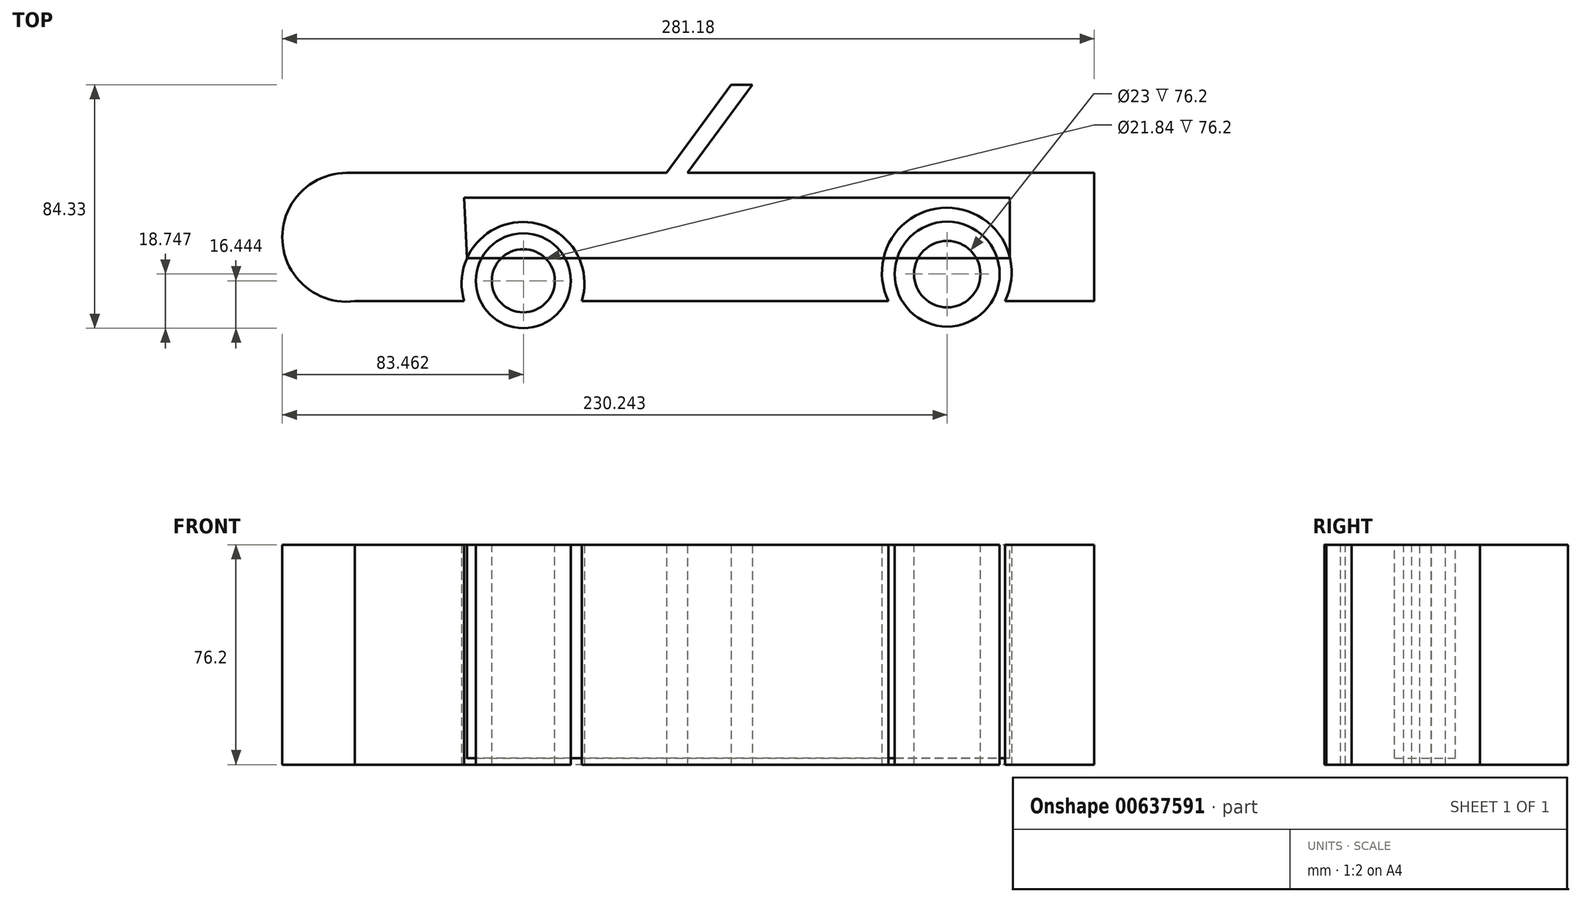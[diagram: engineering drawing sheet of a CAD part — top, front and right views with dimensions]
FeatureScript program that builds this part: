
annotation { "Feature Type Name" : "Feature", "Feature Type Description" : "" }
export const myFeature = defineFeature(function(context is Context, id is Id, definition is map)
    precondition{}
    {
        {
            var Q0;
            Q0=qCreatedBy(makeId("Top.planeOp"),FACE);
            var sketch = newSketch(context, id + "F0", { "sketchPlane" : qUnion([Q0])});
            skLineSegment(sketch, "E0", {"start": v(-131.9, 16.49) * mm, "end": v(-62.3, 16.49) * mm});
            skLineSegment(sketch, "E1", {"start": v(-62.3, 16.49) * mm, "end": v(-39.9, 47.02) * mm});
            skLineSegment(sketch, "E2", {"start": v(-131.9, 16.49) * mm, "end": v(-173.01, 16.49) * mm});
            skLineSegment(sketch, "E3", {"start": v(-170.17, -27.93) * mm, "end": v(-132.31, -27.93) * mm});
            skArc(sketch, "E4", {"start": v(-173.01, 16.49) * mm, "mid": v(-195.27, -7.24) * mm, "end": v(-170.17, -27.93) * mm});
            skArc(sketch, "E5", {"start": v(-91.6, -27.93) * mm, "mid": v(-111.96, -0.49) * mm, "end": v(-132.31, -27.93) * mm});
            skLineSegment(sketch, "E6", {"start": v(-91.6, -27.93) * mm, "end": v(14.63, -27.93) * mm});
            skArc(sketch, "E7", {"start": v(54.93, -27.93) * mm, "mid": v(34.78, 4.42) * mm, "end": v(14.63, -27.93) * mm});
            skLineSegment(sketch, "E8", {"start": v(54.93, -27.93) * mm, "end": v(87.5, -27.93) * mm});
            skLineSegment(sketch, "E9", {"start": v(-62.3, 16.49) * mm, "end": v(85.87, 16.49) * mm});
            skLineSegment(sketch, "E10", {"start": v(85.87, 16.49) * mm, "end": v(85.87, -27.93) * mm});
            skLineSegment(sketch, "E11", {"start": v(-39.9, 47.02) * mm, "end": v(-32.57, 47.02) * mm});
            skLineSegment(sketch, "E12", {"start": v(-32.57, 47.02) * mm, "end": v(-54.96, 16.49) * mm});
            skSolve(sketch);
        }
        {
            var Q0;
            {var subQ3=sQuery(id+"F0.wireOp",EDGE,"E0");Q0=makeQuery(id+"F0.imprint","IMPRINT",FACE,{"disambiguationData":[TD([[makeQuery(id+"F0.imprint","IMPRINT",EDGE,{"derivedFrom":subQ3}),-1.0]])]});}
            var Q1;
            {var subQ0=sQuery(id+"F0.wireOp",EDGE,"E1");Q1=makeQuery(id+"F0.imprint","IMPRINT",FACE,{"disambiguationData":[TD([[makeQuery(id+"F0.imprint","IMPRINT",EDGE,{"derivedFrom":subQ0}),-1.0]])]});}
            extrude(context, id + "F1", {"entities" : qUnion([Q0, Q1]), "depth" : 76.2 * mm, "offsetDistance" : 25.4 * mm});
        }
        {
            var Q0;
            Q0=qCreatedBy(makeId("Top.planeOp"),FACE);
            var sketch = newSketch(context, id + "F2", { "sketchPlane" : qUnion([Q0])});
            skCircle(sketch, "E13", {"center": v(-111.85, -20.87) * mm, "radius": 16.45 * mm});
            skSolve(sketch);
        }
        {
            var Q0;
            Q0=makeQuery(id+"F2.imprint","IMPRINT",FACE,{"disambiguationData":[TD([[makeQuery(id+"F2.imprint","IMPRINT",EDGE,{"derivedFrom":sQuery(id+"F2.wireOp",EDGE,"E13")}),1.0]])]});
            extrude(context, id + "F3", {"entities" : qUnion([Q0]), "depth" : 25.4 * mm, "offsetDistance" : 25.4 * mm});
        }
        {
            var Q0;
            Q0=qCreatedBy(makeId("Top.planeOp"),FACE);
            var sketch = newSketch(context, id + "F4", { "sketchPlane" : qUnion([Q0])});
            skCircle(sketch, "E14", {"center": v(34.93, -18.56) * mm, "radius": 18.17 * mm});
            skSolve(sketch);
        }
        {
            var Q0;
            Q0=makeQuery(id+"F4.imprint","IMPRINT",FACE,{"disambiguationData":[TD([[makeQuery(id+"F4.imprint","IMPRINT",EDGE,{"derivedFrom":sQuery(id+"F4.wireOp",EDGE,"E14")}),1.0]])]});
            extrude(context, id + "F5", {"entities" : qUnion([Q0]), "depth" : 25.4 * mm, "offsetDistance" : 25.4 * mm});
        }
        {
            var Q0;
            Q0=makeQuery(id+"F3.opExtrude","CAP_FACE",FACE,{"disambiguationData":[OSD([sQuery(id+"F2.wireOp",EDGE,"E13")])],"isStart":false});
            extrude(context, id + "F6", {"entities" : qUnion([Q0]), "operationType" : NewBodyOperationType.ADD, "depth" : 25.4 * mm, "offsetDistance" : 25.4 * mm});
        }
        {
            var Q0;
            Q0=makeQuery(id+"F6.opExtrude","CAP_FACE",FACE,{"disambiguationData":[OSD([sQuery(id+"F2.wireOp",EDGE,"E13")])],"isStart":false});
            extrude(context, id + "F7", {"entities" : qUnion([Q0]), "operationType" : NewBodyOperationType.ADD, "depth" : 25.4 * mm, "offsetDistance" : 25.4 * mm});
        }
        {
            var Q0;
            Q0=makeQuery(id+"F5.opExtrude","CAP_FACE",FACE,{"disambiguationData":[OSD([sQuery(id+"F4.wireOp",EDGE,"E14")])],"isStart":false});
            extrude(context, id + "F8", {"entities" : qUnion([Q0]), "operationType" : NewBodyOperationType.ADD, "depth" : 25.4 * mm, "offsetDistance" : 25.4 * mm});
        }
        {
            var Q0;
            Q0=makeQuery(id+"F8.opExtrude","CAP_FACE",FACE,{"disambiguationData":[OSD([sQuery(id+"F4.wireOp",EDGE,"E14")])],"isStart":false});
            extrude(context, id + "F9", {"entities" : qUnion([Q0]), "operationType" : NewBodyOperationType.ADD, "depth" : 25.4 * mm, "offsetDistance" : 25.4 * mm});
        }
        {
            var Q0;
            Q0=makeQuery(id+"F7.opExtrude","CAP_FACE",FACE,{"disambiguationData":[OSD([sQuery(id+"F2.wireOp",EDGE,"E13")])],"isStart":false});
            var sketch = newSketch(context, id + "F10", { "sketchPlane" : qUnion([Q0])});
            skCircle(sketch, "E15", {"center": v(-111.85, -20.87) * mm, "radius": 10.92 * mm});
            skSolve(sketch);
        }
        {
            var Q0;
            Q0 = qSketchRegion(id + "F10", true);
            extrude(context, id + "F11", {"entities" : qUnion([Q0]), "operationType" : NewBodyOperationType.REMOVE, "oppositeDirection" : true, "depth" : 134.11 * mm, "offsetDistance" : 25.4 * mm});
        }
        {
            var Q0;
            Q0=makeQuery(id+"F9.opExtrude","CAP_FACE",FACE,{"disambiguationData":[OSD([sQuery(id+"F4.wireOp",EDGE,"E14")])],"isStart":false});
            var sketch = newSketch(context, id + "F12", { "sketchPlane" : qUnion([Q0])});
            skCircle(sketch, "E16", {"center": v(34.93, -18.56) * mm, "radius": 11.5 * mm});
            skSolve(sketch);
        }
        {
            var Q0;
            Q0=makeQuery(id+"F12.imprint","IMPRINT",FACE,{"disambiguationData":[TD([[makeQuery(id+"F12.imprint","IMPRINT",EDGE,{"derivedFrom":sQuery(id+"F12.wireOp",EDGE,"E16")}),1.0]])]});
            extrude(context, id + "F13", {"entities" : qUnion([Q0]), "operationType" : NewBodyOperationType.REMOVE, "oppositeDirection" : true, "depth" : 76.2 * mm, "offsetDistance" : 25.4 * mm});
        }
        {
            var Q0;
            Q0=makeQuery(id+"F1.opExtrude","CAP_FACE",FACE,{"disambiguationData":[OSD([sQuery(id+"F0.wireOp",EDGE,"E0"),sQuery(id+"F0.wireOp",EDGE,"E1"),sQuery(id+"F0.wireOp",EDGE,"E2"),sQuery(id+"F0.wireOp",EDGE,"E3"),sQuery(id+"F0.wireOp",EDGE,"E4"),sQuery(id+"F0.wireOp",EDGE,"E5"),sQuery(id+"F0.wireOp",EDGE,"E6"),sQuery(id+"F0.wireOp",EDGE,"E7"),sQuery(id+"F0.wireOp",EDGE,"E8"),sQuery(id+"F0.wireOp",EDGE,"E9"),sQuery(id+"F0.wireOp",EDGE,"E10"),sQuery(id+"F0.wireOp",EDGE,"E11"),sQuery(id+"F0.wireOp",EDGE,"E12")])],"isStart":false});
            var sketch = newSketch(context, id + "F14", { "sketchPlane" : qUnion([Q0])});
            skLineSegment(sketch, "E17", {"start": v(-131.37, -13.05) * mm, "end": v(56.67, -13.05) * mm});
            skLineSegment(sketch, "E18", {"start": v(56.67, -13.05) * mm, "end": v(56.67, 7.96) * mm});
            skLineSegment(sketch, "E19", {"start": v(56.67, 7.96) * mm, "end": v(-132.31, 7.96) * mm});
            skLineSegment(sketch, "E20", {"start": v(-132.31, 7.96) * mm, "end": v(-131.37, -13.05) * mm});
            skSolve(sketch);
        }
        {
            var Q0;
            Q0 = qSketchRegion(id + "F14", true);
            extrude(context, id + "F15", {"entities" : qUnion([Q0]), "oppositeDirection" : true, "depth" : 73.9 * mm, "offsetDistance" : 25.4 * mm});
        }
    });
